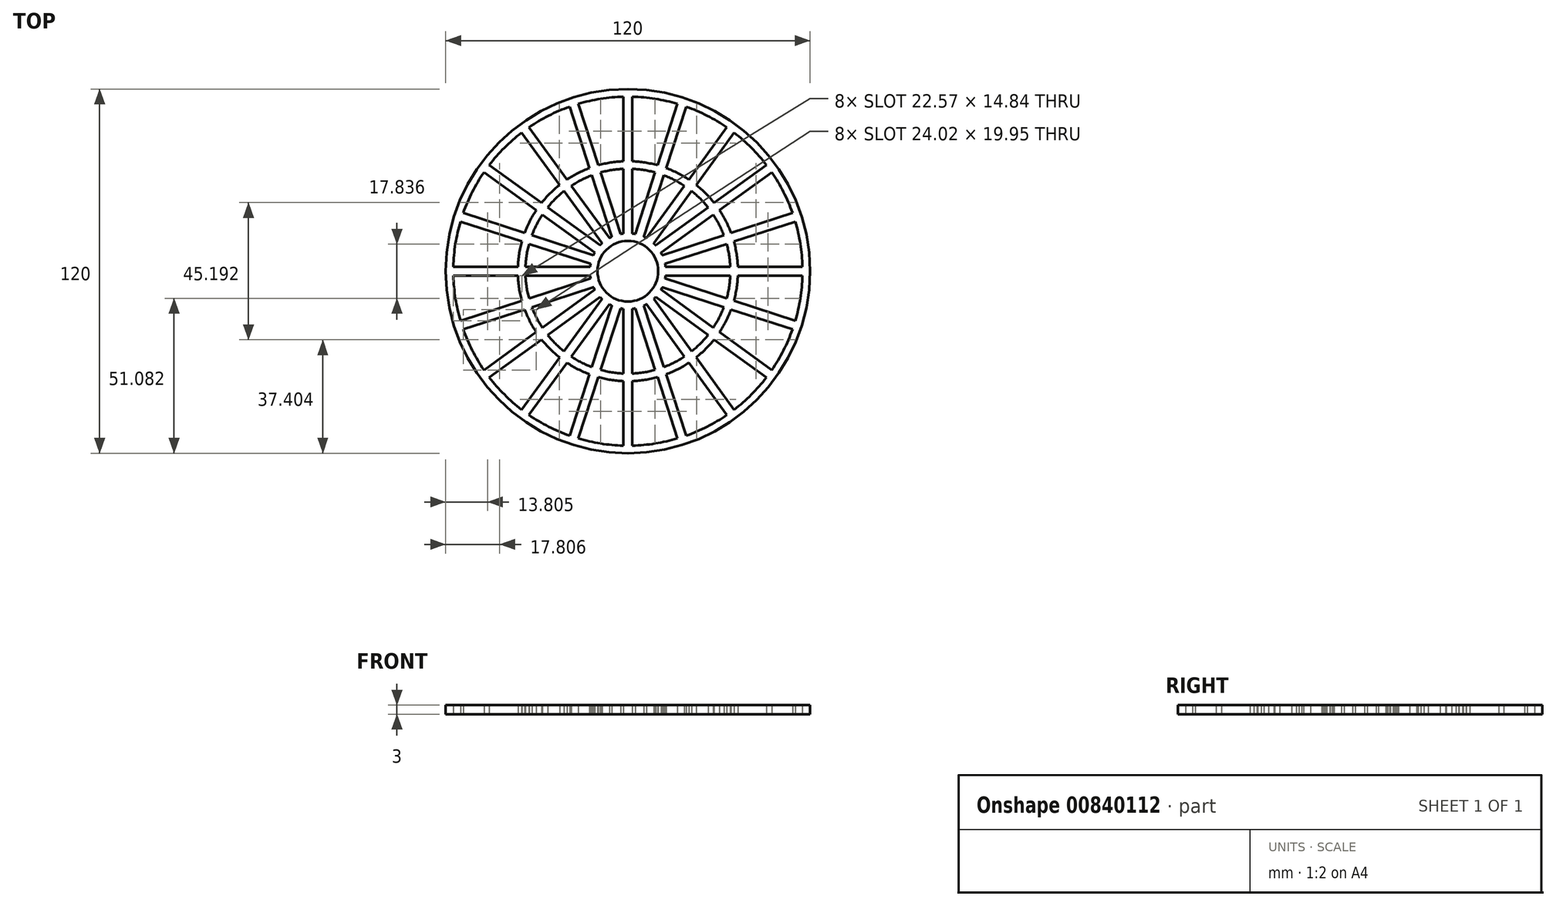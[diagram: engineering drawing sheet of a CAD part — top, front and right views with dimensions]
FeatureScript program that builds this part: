
annotation { "Feature Type Name" : "Feature", "Feature Type Description" : "" }
export const myFeature = defineFeature(function(context is Context, id is Id, definition is map)
    precondition{}
    {
        {
            var Q0;
            Q0=qCreatedBy(makeId("Top.planeOp"),FACE);
            var sketch = newSketch(context, id + "F0", { "sketchPlane" : qUnion([Q0])});
            skCircle(sketch, "E0", {"center": v(0, 0) * mm, "radius": 60 * mm});
            skCircle(sketch, "E1", {"center": v(0, 0) * mm, "radius": 10 * mm});
            skCircle(sketch, "E2", {"center": v(0, 0) * mm, "radius": 12.5 * mm});
            skCircle(sketch, "E3", {"center": v(0, 0) * mm, "radius": 57.5 * mm});
            skLineSegment(sketch, "E4.bottom", {"start": v(-57.5, 1.5) * mm, "end": v(0, 1.5) * mm});
            skLineSegment(sketch, "E4.top", {"start": v(-57.5, -1.5) * mm, "end": v(0, -1.5) * mm});
            skLineSegment(sketch, "E4.left", {"start": v(-57.5, 1.5) * mm, "end": v(-57.5, -1.5) * mm});
            skLineSegment(sketch, "E4.right", {"start": v(0, 1.5) * mm, "end": v(0, -1.5) * mm});
            skLineSegment(sketch, "E5.1.0", {"start": v(-55.15, -16.34) * mm, "end": v(-0.46, 1.43) * mm});
            skLineSegment(sketch, "E5.1.1", {"start": v(-54.22, -19.2) * mm, "end": v(0.46, -1.43) * mm});
            skLineSegment(sketch, "E5.2.0", {"start": v(-47.4, -32.58) * mm, "end": v(-0.88, 1.21) * mm});
            skLineSegment(sketch, "E5.2.1", {"start": v(-45.64, -35.01) * mm, "end": v(0.88, -1.21) * mm});
            skLineSegment(sketch, "E5.3.0", {"start": v(-35.01, -45.64) * mm, "end": v(-1.21, 0.88) * mm});
            skLineSegment(sketch, "E5.3.1", {"start": v(-32.58, -47.4) * mm, "end": v(1.21, -0.88) * mm});
            skLineSegment(sketch, "E5.4.0", {"start": v(-19.2, -54.22) * mm, "end": v(-1.43, 0.46) * mm});
            skLineSegment(sketch, "E5.4.1", {"start": v(-16.34, -55.15) * mm, "end": v(1.43, -0.46) * mm});
            skLineSegment(sketch, "E5.5.0", {"start": v(-1.5, -57.5) * mm, "end": v(-1.5, 0) * mm});
            skLineSegment(sketch, "E5.5.1", {"start": v(1.5, -57.5) * mm, "end": v(1.5, 0) * mm});
            skLineSegment(sketch, "E5.6.0", {"start": v(16.34, -55.15) * mm, "end": v(-1.43, -0.46) * mm});
            skLineSegment(sketch, "E5.6.1", {"start": v(19.2, -54.22) * mm, "end": v(1.43, 0.46) * mm});
            skLineSegment(sketch, "E5.7.0", {"start": v(32.58, -47.4) * mm, "end": v(-1.21, -0.88) * mm});
            skLineSegment(sketch, "E5.7.1", {"start": v(35.01, -45.64) * mm, "end": v(1.21, 0.88) * mm});
            skLineSegment(sketch, "E5.8.0", {"start": v(45.64, -35.01) * mm, "end": v(-0.88, -1.21) * mm});
            skLineSegment(sketch, "E5.8.1", {"start": v(47.4, -32.58) * mm, "end": v(0.88, 1.21) * mm});
            skLineSegment(sketch, "E5.9.0", {"start": v(54.22, -19.2) * mm, "end": v(-0.46, -1.43) * mm});
            skLineSegment(sketch, "E5.9.1", {"start": v(55.15, -16.34) * mm, "end": v(0.46, 1.43) * mm});
            skLineSegment(sketch, "E5.10.0", {"start": v(57.5, -1.5) * mm, "end": v(0, -1.5) * mm});
            skLineSegment(sketch, "E5.10.1", {"start": v(57.5, 1.5) * mm, "end": v(0, 1.5) * mm});
            skLineSegment(sketch, "E5.11.0", {"start": v(55.15, 16.34) * mm, "end": v(0.46, -1.43) * mm});
            skLineSegment(sketch, "E5.11.1", {"start": v(54.22, 19.2) * mm, "end": v(-0.46, 1.43) * mm});
            skLineSegment(sketch, "E5.12.0", {"start": v(47.4, 32.58) * mm, "end": v(0.88, -1.21) * mm});
            skLineSegment(sketch, "E5.12.1", {"start": v(45.64, 35.01) * mm, "end": v(-0.88, 1.21) * mm});
            skLineSegment(sketch, "E5.13.0", {"start": v(35.01, 45.64) * mm, "end": v(1.21, -0.88) * mm});
            skLineSegment(sketch, "E5.13.1", {"start": v(32.58, 47.4) * mm, "end": v(-1.21, 0.88) * mm});
            skLineSegment(sketch, "E5.14.0", {"start": v(19.2, 54.22) * mm, "end": v(1.43, -0.46) * mm});
            skLineSegment(sketch, "E5.14.1", {"start": v(16.34, 55.15) * mm, "end": v(-1.43, 0.46) * mm});
            skCircle(sketch, "E6", {"center": v(0, 0) * mm, "radius": 33.75 * mm});
            skCircle(sketch, "E7", {"center": v(0, 0) * mm, "radius": 36.25 * mm});
            skLineSegment(sketch, "E8.1.15.0", {"start": v(1.5, 57.5) * mm, "end": v(1.5, 0) * mm});
            skLineSegment(sketch, "E8.3.15.0", {"start": v(-1.5, 57.5) * mm, "end": v(-1.5, 0) * mm});
            skLineSegment(sketch, "E8.1.16.0", {"start": v(-16.34, 55.15) * mm, "end": v(1.43, 0.46) * mm});
            skLineSegment(sketch, "E8.3.16.0", {"start": v(-19.2, 54.22) * mm, "end": v(-1.43, -0.46) * mm});
            skLineSegment(sketch, "E8.1.17.0", {"start": v(-32.58, 47.4) * mm, "end": v(1.21, 0.88) * mm});
            skLineSegment(sketch, "E8.3.17.0", {"start": v(-35.01, 45.64) * mm, "end": v(-1.21, -0.88) * mm});
            skLineSegment(sketch, "E8.1.18.0", {"start": v(-45.64, 35.01) * mm, "end": v(0.88, 1.21) * mm});
            skLineSegment(sketch, "E8.3.18.0", {"start": v(-47.4, 32.58) * mm, "end": v(-0.88, -1.21) * mm});
            skLineSegment(sketch, "E8.1.19.0", {"start": v(-54.22, 19.2) * mm, "end": v(0.46, 1.43) * mm});
            skLineSegment(sketch, "E8.3.19.0", {"start": v(-55.15, 16.34) * mm, "end": v(-0.46, -1.43) * mm});
            skSolve(sketch);
        }
        {
            var Q0;
            Q0=qCreatedBy(makeId("Top.planeOp"),FACE);
            var sketch = newSketch(context, id + "F1", { "sketchPlane" : qUnion([Q0])});
            skCircle(sketch, "E9", {"center": v(0, 0) * mm, "radius": 60 * mm});
            skCircle(sketch, "E10", {"center": v(0, 0) * mm, "radius": 10 * mm});
            skSolve(sketch);
        }
        {
            var Q0;
            Q0=makeQuery(id+"F1.imprint","IMPRINT",FACE,{"disambiguationData":[TD([[makeQuery(id+"F1.imprint","IMPRINT",EDGE,{"derivedFrom":sQuery(id+"F1.wireOp",EDGE,"E9")}),1.0]])]});
            extrude(context, id + "F2", {"entities" : qUnion([Q0]), "depth" : 3 * mm, "offsetDistance" : 25 * mm});
        }
        {
            var Q0;
            {var subQ0=sQuery(id+"F0.wireOp",EDGE,"E5.11.1");var subQ1=sQuery(id+"F0.wireOp",EDGE,"E2");var subQ2=makeQuery(id+"F0.imprint","INTERSECT",VERTEX,{"derivedFrom":[subQ1,subQ0]});Q0=makeQuery(id+"F0.imprint","IMPRINT",FACE,{"disambiguationData":[TD([[makeQuery(id+"F0.imprint","IMPRINT",EDGE,{"disambiguationData":[TD([[subQ2,-1.0]])],"derivedFrom":subQ1}),-1.0]])]});}
            var Q1;
            {var subQ0=sQuery(id+"F0.wireOp",EDGE,"E5.12.1");var subQ1=sQuery(id+"F0.wireOp",EDGE,"E2");var subQ2=makeQuery(id+"F0.imprint","INTERSECT",VERTEX,{"derivedFrom":[subQ1,subQ0]});Q1=makeQuery(id+"F0.imprint","IMPRINT",FACE,{"disambiguationData":[TD([[makeQuery(id+"F0.imprint","IMPRINT",EDGE,{"disambiguationData":[TD([[subQ2,-1.0]])],"derivedFrom":subQ1}),-1.0]])]});}
            var Q2;
            {var subQ0=sQuery(id+"F0.wireOp",EDGE,"E5.13.1");var subQ1=sQuery(id+"F0.wireOp",EDGE,"E2");var subQ2=makeQuery(id+"F0.imprint","INTERSECT",VERTEX,{"derivedFrom":[subQ1,subQ0]});Q2=makeQuery(id+"F0.imprint","IMPRINT",FACE,{"disambiguationData":[TD([[makeQuery(id+"F0.imprint","IMPRINT",EDGE,{"disambiguationData":[TD([[subQ2,-1.0]])],"derivedFrom":subQ1}),-1.0]])]});}
            var Q3;
            {var subQ0=sQuery(id+"F0.wireOp",EDGE,"E5.14.1");var subQ1=sQuery(id+"F0.wireOp",EDGE,"E2");var subQ2=makeQuery(id+"F0.imprint","INTERSECT",VERTEX,{"derivedFrom":[subQ1,subQ0]});Q3=makeQuery(id+"F0.imprint","IMPRINT",FACE,{"disambiguationData":[TD([[makeQuery(id+"F0.imprint","IMPRINT",EDGE,{"disambiguationData":[TD([[subQ2,-1.0]])],"derivedFrom":subQ1}),-1.0]])]});}
            var Q4;
            {var subQ0=sQuery(id+"F0.wireOp",EDGE,"E4.top");var subQ1=sQuery(id+"F0.wireOp",EDGE,"E2");var subQ2=makeQuery(id+"F0.imprint","INTERSECT",VERTEX,{"derivedFrom":[subQ1,subQ0]});Q4=makeQuery(id+"F0.imprint","IMPRINT",FACE,{"disambiguationData":[TD([[makeQuery(id+"F0.imprint","IMPRINT",EDGE,{"disambiguationData":[TD([[subQ2,-1.0]])],"derivedFrom":subQ1}),-1.0]])]});}
            var Q5;
            {var subQ0=sQuery(id+"F0.wireOp",EDGE,"E5.1.1");var subQ1=sQuery(id+"F0.wireOp",EDGE,"E2");var subQ2=makeQuery(id+"F0.imprint","INTERSECT",VERTEX,{"derivedFrom":[subQ1,subQ0]});Q5=makeQuery(id+"F0.imprint","IMPRINT",FACE,{"disambiguationData":[TD([[makeQuery(id+"F0.imprint","IMPRINT",EDGE,{"disambiguationData":[TD([[subQ2,-1.0]])],"derivedFrom":subQ1}),-1.0]])]});}
            var Q6;
            {var subQ0=sQuery(id+"F0.wireOp",EDGE,"E5.2.1");var subQ1=sQuery(id+"F0.wireOp",EDGE,"E2");var subQ2=makeQuery(id+"F0.imprint","INTERSECT",VERTEX,{"derivedFrom":[subQ1,subQ0]});Q6=makeQuery(id+"F0.imprint","IMPRINT",FACE,{"disambiguationData":[TD([[makeQuery(id+"F0.imprint","IMPRINT",EDGE,{"disambiguationData":[TD([[subQ2,-1.0]])],"derivedFrom":subQ1}),-1.0]])]});}
            var Q7;
            {var subQ0=sQuery(id+"F0.wireOp",EDGE,"E5.3.1");var subQ1=sQuery(id+"F0.wireOp",EDGE,"E2");var subQ2=makeQuery(id+"F0.imprint","INTERSECT",VERTEX,{"derivedFrom":[subQ1,subQ0]});Q7=makeQuery(id+"F0.imprint","IMPRINT",FACE,{"disambiguationData":[TD([[makeQuery(id+"F0.imprint","IMPRINT",EDGE,{"disambiguationData":[TD([[subQ2,-1.0]])],"derivedFrom":subQ1}),-1.0]])]});}
            var Q8;
            {var subQ0=sQuery(id+"F0.wireOp",EDGE,"E5.4.1");var subQ1=sQuery(id+"F0.wireOp",EDGE,"E2");var subQ2=makeQuery(id+"F0.imprint","INTERSECT",VERTEX,{"derivedFrom":[subQ1,subQ0]});Q8=makeQuery(id+"F0.imprint","IMPRINT",FACE,{"disambiguationData":[TD([[makeQuery(id+"F0.imprint","IMPRINT",EDGE,{"disambiguationData":[TD([[subQ2,-1.0]])],"derivedFrom":subQ1}),-1.0]])]});}
            var Q9;
            {var subQ0=sQuery(id+"F0.wireOp",EDGE,"E5.5.1");var subQ1=sQuery(id+"F0.wireOp",EDGE,"E2");var subQ2=makeQuery(id+"F0.imprint","INTERSECT",VERTEX,{"derivedFrom":[subQ1,subQ0]});Q9=makeQuery(id+"F0.imprint","IMPRINT",FACE,{"disambiguationData":[TD([[makeQuery(id+"F0.imprint","IMPRINT",EDGE,{"disambiguationData":[TD([[subQ2,-1.0]])],"derivedFrom":subQ1}),-1.0]])]});}
            var Q10;
            {var subQ0=sQuery(id+"F0.wireOp",EDGE,"E5.6.1");var subQ1=sQuery(id+"F0.wireOp",EDGE,"E2");var subQ2=makeQuery(id+"F0.imprint","INTERSECT",VERTEX,{"derivedFrom":[subQ1,subQ0]});Q10=makeQuery(id+"F0.imprint","IMPRINT",FACE,{"disambiguationData":[TD([[makeQuery(id+"F0.imprint","IMPRINT",EDGE,{"disambiguationData":[TD([[subQ2,-1.0]])],"derivedFrom":subQ1}),-1.0]])]});}
            var Q11;
            {var subQ0=sQuery(id+"F0.wireOp",EDGE,"E5.8.0");var subQ1=sQuery(id+"F0.wireOp",EDGE,"E2");var subQ2=makeQuery(id+"F0.imprint","INTERSECT",VERTEX,{"derivedFrom":[subQ1,subQ0]});Q11=makeQuery(id+"F0.imprint","IMPRINT",FACE,{"disambiguationData":[TD([[makeQuery(id+"F0.imprint","IMPRINT",EDGE,{"disambiguationData":[TD([[subQ2,1.0]])],"derivedFrom":subQ1}),-1.0]])]});}
            var Q12;
            {var subQ0=sQuery(id+"F0.wireOp",EDGE,"E5.8.1");var subQ1=sQuery(id+"F0.wireOp",EDGE,"E2");var subQ2=makeQuery(id+"F0.imprint","INTERSECT",VERTEX,{"derivedFrom":[subQ1,subQ0]});Q12=makeQuery(id+"F0.imprint","IMPRINT",FACE,{"disambiguationData":[TD([[makeQuery(id+"F0.imprint","IMPRINT",EDGE,{"disambiguationData":[TD([[subQ2,-1.0]])],"derivedFrom":subQ1}),-1.0]])]});}
            var Q13;
            {var subQ0=sQuery(id+"F0.wireOp",EDGE,"E5.10.1");var subQ1=sQuery(id+"F0.wireOp",EDGE,"E2");var subQ2=makeQuery(id+"F0.imprint","INTERSECT",VERTEX,{"derivedFrom":[subQ1,subQ0]});Q13=makeQuery(id+"F0.imprint","IMPRINT",FACE,{"disambiguationData":[TD([[makeQuery(id+"F0.imprint","IMPRINT",EDGE,{"disambiguationData":[TD([[subQ2,-1.0]])],"derivedFrom":subQ1}),-1.0]])]});}
            var Q14;
            {var subQ0=sQuery(id+"F0.wireOp",EDGE,"E5.9.1");var subQ1=sQuery(id+"F0.wireOp",EDGE,"E2");var subQ2=makeQuery(id+"F0.imprint","INTERSECT",VERTEX,{"derivedFrom":[subQ1,subQ0]});Q14=makeQuery(id+"F0.imprint","IMPRINT",FACE,{"disambiguationData":[TD([[makeQuery(id+"F0.imprint","IMPRINT",EDGE,{"disambiguationData":[TD([[subQ2,-1.0]])],"derivedFrom":subQ1}),-1.0]])]});}
            var Q15;
            {var subQ0=sQuery(id+"F0.wireOp",EDGE,"E8.3.19.0");var subQ1=sQuery(id+"F0.wireOp",EDGE,"E2");var subQ2=makeQuery(id+"F0.imprint","INTERSECT",VERTEX,{"derivedFrom":[subQ1,subQ0]});Q15=makeQuery(id+"F0.imprint","IMPRINT",FACE,{"disambiguationData":[TD([[makeQuery(id+"F0.imprint","IMPRINT",EDGE,{"disambiguationData":[TD([[subQ2,-1.0]])],"derivedFrom":subQ1}),-1.0]])]});}
            var Q16;
            {var subQ0=sQuery(id+"F0.wireOp",EDGE,"E8.3.18.0");var subQ1=sQuery(id+"F0.wireOp",EDGE,"E2");var subQ2=makeQuery(id+"F0.imprint","INTERSECT",VERTEX,{"derivedFrom":[subQ1,subQ0]});Q16=makeQuery(id+"F0.imprint","IMPRINT",FACE,{"disambiguationData":[TD([[makeQuery(id+"F0.imprint","IMPRINT",EDGE,{"disambiguationData":[TD([[subQ2,-1.0]])],"derivedFrom":subQ1}),-1.0]])]});}
            var Q17;
            {var subQ0=sQuery(id+"F0.wireOp",EDGE,"E8.3.17.0");var subQ1=sQuery(id+"F0.wireOp",EDGE,"E2");var subQ2=makeQuery(id+"F0.imprint","INTERSECT",VERTEX,{"derivedFrom":[subQ1,subQ0]});Q17=makeQuery(id+"F0.imprint","IMPRINT",FACE,{"disambiguationData":[TD([[makeQuery(id+"F0.imprint","IMPRINT",EDGE,{"disambiguationData":[TD([[subQ2,-1.0]])],"derivedFrom":subQ1}),-1.0]])]});}
            var Q18;
            {var subQ0=sQuery(id+"F0.wireOp",EDGE,"E8.3.16.0");var subQ1=sQuery(id+"F0.wireOp",EDGE,"E2");var subQ2=makeQuery(id+"F0.imprint","INTERSECT",VERTEX,{"derivedFrom":[subQ1,subQ0]});Q18=makeQuery(id+"F0.imprint","IMPRINT",FACE,{"disambiguationData":[TD([[makeQuery(id+"F0.imprint","IMPRINT",EDGE,{"disambiguationData":[TD([[subQ2,-1.0]])],"derivedFrom":subQ1}),-1.0]])]});}
            var Q19;
            {var subQ0=sQuery(id+"F0.wireOp",EDGE,"E8.3.15.0");var subQ1=sQuery(id+"F0.wireOp",EDGE,"E2");var subQ2=makeQuery(id+"F0.imprint","INTERSECT",VERTEX,{"derivedFrom":[subQ1,subQ0]});Q19=makeQuery(id+"F0.imprint","IMPRINT",FACE,{"disambiguationData":[TD([[makeQuery(id+"F0.imprint","IMPRINT",EDGE,{"disambiguationData":[TD([[subQ2,-1.0]])],"derivedFrom":subQ1}),-1.0]])]});}
            var Q20;
            {var subQ0=sQuery(id+"F0.wireOp",EDGE,"E8.3.19.0");var subQ1=sQuery(id+"F0.wireOp",EDGE,"E3");var subQ2=makeQuery(id+"F0.imprint","INTERSECT",VERTEX,{"derivedFrom":[subQ1,subQ0]});Q20=makeQuery(id+"F0.imprint","IMPRINT",FACE,{"disambiguationData":[TD([[makeQuery(id+"F0.imprint","IMPRINT",EDGE,{"disambiguationData":[TD([[subQ2,-1.0]])],"derivedFrom":subQ1}),1.0]])]});}
            var Q21;
            {var subQ0=sQuery(id+"F0.wireOp",EDGE,"E5.1.0");var subQ1=sQuery(id+"F0.wireOp",EDGE,"E3");var subQ2=makeQuery(id+"F0.imprint","INTERSECT",VERTEX,{"derivedFrom":[subQ1,subQ0]});Q21=makeQuery(id+"F0.imprint","IMPRINT",FACE,{"disambiguationData":[TD([[makeQuery(id+"F0.imprint","IMPRINT",EDGE,{"disambiguationData":[TD([[subQ2,1.0]])],"derivedFrom":subQ1}),1.0]])]});}
            var Q22;
            {var subQ0=sQuery(id+"F0.wireOp",EDGE,"E5.1.1");var subQ1=sQuery(id+"F0.wireOp",EDGE,"E3");var subQ2=makeQuery(id+"F0.imprint","INTERSECT",VERTEX,{"derivedFrom":[subQ1,subQ0]});Q22=makeQuery(id+"F0.imprint","IMPRINT",FACE,{"disambiguationData":[TD([[makeQuery(id+"F0.imprint","IMPRINT",EDGE,{"disambiguationData":[TD([[subQ2,-1.0]])],"derivedFrom":subQ1}),1.0]])]});}
            var Q23;
            {var subQ0=sQuery(id+"F0.wireOp",EDGE,"E5.2.1");var subQ1=sQuery(id+"F0.wireOp",EDGE,"E3");var subQ2=makeQuery(id+"F0.imprint","INTERSECT",VERTEX,{"derivedFrom":[subQ1,subQ0]});Q23=makeQuery(id+"F0.imprint","IMPRINT",FACE,{"disambiguationData":[TD([[makeQuery(id+"F0.imprint","IMPRINT",EDGE,{"disambiguationData":[TD([[subQ2,-1.0]])],"derivedFrom":subQ1}),1.0]])]});}
            var Q24;
            {var subQ0=sQuery(id+"F0.wireOp",EDGE,"E5.3.1");var subQ1=sQuery(id+"F0.wireOp",EDGE,"E3");var subQ2=makeQuery(id+"F0.imprint","INTERSECT",VERTEX,{"derivedFrom":[subQ1,subQ0]});Q24=makeQuery(id+"F0.imprint","IMPRINT",FACE,{"disambiguationData":[TD([[makeQuery(id+"F0.imprint","IMPRINT",EDGE,{"disambiguationData":[TD([[subQ2,-1.0]])],"derivedFrom":subQ1}),1.0]])]});}
            var Q25;
            {var subQ0=sQuery(id+"F0.wireOp",EDGE,"E5.4.1");var subQ1=sQuery(id+"F0.wireOp",EDGE,"E3");var subQ2=makeQuery(id+"F0.imprint","INTERSECT",VERTEX,{"derivedFrom":[subQ1,subQ0]});Q25=makeQuery(id+"F0.imprint","IMPRINT",FACE,{"disambiguationData":[TD([[makeQuery(id+"F0.imprint","IMPRINT",EDGE,{"disambiguationData":[TD([[subQ2,-1.0]])],"derivedFrom":subQ1}),1.0]])]});}
            var Q26;
            {var subQ0=sQuery(id+"F0.wireOp",EDGE,"E5.5.1");var subQ1=sQuery(id+"F0.wireOp",EDGE,"E3");var subQ2=makeQuery(id+"F0.imprint","INTERSECT",VERTEX,{"derivedFrom":[subQ1,subQ0]});Q26=makeQuery(id+"F0.imprint","IMPRINT",FACE,{"disambiguationData":[TD([[makeQuery(id+"F0.imprint","IMPRINT",EDGE,{"disambiguationData":[TD([[subQ2,-1.0]])],"derivedFrom":subQ1}),1.0]])]});}
            var Q27;
            {var subQ0=sQuery(id+"F0.wireOp",EDGE,"E5.6.1");var subQ1=sQuery(id+"F0.wireOp",EDGE,"E3");var subQ2=makeQuery(id+"F0.imprint","INTERSECT",VERTEX,{"derivedFrom":[subQ1,subQ0]});Q27=makeQuery(id+"F0.imprint","IMPRINT",FACE,{"disambiguationData":[TD([[makeQuery(id+"F0.imprint","IMPRINT",EDGE,{"disambiguationData":[TD([[subQ2,-1.0]])],"derivedFrom":subQ1}),1.0]])]});}
            var Q28;
            {var subQ0=sQuery(id+"F0.wireOp",EDGE,"E5.7.1");var subQ1=sQuery(id+"F0.wireOp",EDGE,"E3");var subQ2=makeQuery(id+"F0.imprint","INTERSECT",VERTEX,{"derivedFrom":[subQ1,subQ0]});Q28=makeQuery(id+"F0.imprint","IMPRINT",FACE,{"disambiguationData":[TD([[makeQuery(id+"F0.imprint","IMPRINT",EDGE,{"disambiguationData":[TD([[subQ2,-1.0]])],"derivedFrom":subQ1}),1.0]])]});}
            var Q29;
            {var subQ0=sQuery(id+"F0.wireOp",EDGE,"E5.8.1");var subQ1=sQuery(id+"F0.wireOp",EDGE,"E3");var subQ2=makeQuery(id+"F0.imprint","INTERSECT",VERTEX,{"derivedFrom":[subQ1,subQ0]});Q29=makeQuery(id+"F0.imprint","IMPRINT",FACE,{"disambiguationData":[TD([[makeQuery(id+"F0.imprint","IMPRINT",EDGE,{"disambiguationData":[TD([[subQ2,-1.0]])],"derivedFrom":subQ1}),1.0]])]});}
            var Q30;
            {var subQ0=sQuery(id+"F0.wireOp",EDGE,"E5.9.1");var subQ1=sQuery(id+"F0.wireOp",EDGE,"E3");var subQ2=makeQuery(id+"F0.imprint","INTERSECT",VERTEX,{"derivedFrom":[subQ1,subQ0]});Q30=makeQuery(id+"F0.imprint","IMPRINT",FACE,{"disambiguationData":[TD([[makeQuery(id+"F0.imprint","IMPRINT",EDGE,{"disambiguationData":[TD([[subQ2,-1.0]])],"derivedFrom":subQ1}),1.0]])]});}
            var Q31;
            {var subQ0=sQuery(id+"F0.wireOp",EDGE,"E5.11.0");var subQ1=sQuery(id+"F0.wireOp",EDGE,"E3");var subQ2=makeQuery(id+"F0.imprint","INTERSECT",VERTEX,{"derivedFrom":[subQ1,subQ0]});Q31=makeQuery(id+"F0.imprint","IMPRINT",FACE,{"disambiguationData":[TD([[makeQuery(id+"F0.imprint","IMPRINT",EDGE,{"disambiguationData":[TD([[subQ2,1.0]])],"derivedFrom":subQ1}),1.0]])]});}
            var Q32;
            {var subQ0=sQuery(id+"F0.wireOp",EDGE,"E5.11.1");var subQ1=sQuery(id+"F0.wireOp",EDGE,"E3");var subQ2=makeQuery(id+"F0.imprint","INTERSECT",VERTEX,{"derivedFrom":[subQ1,subQ0]});Q32=makeQuery(id+"F0.imprint","IMPRINT",FACE,{"disambiguationData":[TD([[makeQuery(id+"F0.imprint","IMPRINT",EDGE,{"disambiguationData":[TD([[subQ2,-1.0]])],"derivedFrom":subQ1}),1.0]])]});}
            var Q33;
            {var subQ0=sQuery(id+"F0.wireOp",EDGE,"E5.12.1");var subQ1=sQuery(id+"F0.wireOp",EDGE,"E3");var subQ2=makeQuery(id+"F0.imprint","INTERSECT",VERTEX,{"derivedFrom":[subQ1,subQ0]});Q33=makeQuery(id+"F0.imprint","IMPRINT",FACE,{"disambiguationData":[TD([[makeQuery(id+"F0.imprint","IMPRINT",EDGE,{"disambiguationData":[TD([[subQ2,-1.0]])],"derivedFrom":subQ1}),1.0]])]});}
            var Q34;
            {var subQ0=sQuery(id+"F0.wireOp",EDGE,"E5.13.1");var subQ1=sQuery(id+"F0.wireOp",EDGE,"E3");var subQ2=makeQuery(id+"F0.imprint","INTERSECT",VERTEX,{"derivedFrom":[subQ1,subQ0]});Q34=makeQuery(id+"F0.imprint","IMPRINT",FACE,{"disambiguationData":[TD([[makeQuery(id+"F0.imprint","IMPRINT",EDGE,{"disambiguationData":[TD([[subQ2,-1.0]])],"derivedFrom":subQ1}),1.0]])]});}
            var Q35;
            {var subQ0=sQuery(id+"F0.wireOp",EDGE,"E5.14.1");var subQ1=sQuery(id+"F0.wireOp",EDGE,"E3");var subQ2=makeQuery(id+"F0.imprint","INTERSECT",VERTEX,{"derivedFrom":[subQ1,subQ0]});Q35=makeQuery(id+"F0.imprint","IMPRINT",FACE,{"disambiguationData":[TD([[makeQuery(id+"F0.imprint","IMPRINT",EDGE,{"disambiguationData":[TD([[subQ2,-1.0]])],"derivedFrom":subQ1}),1.0]])]});}
            var Q36;
            {var subQ0=sQuery(id+"F0.wireOp",EDGE,"E8.3.15.0");var subQ1=sQuery(id+"F0.wireOp",EDGE,"E3");var subQ2=makeQuery(id+"F0.imprint","INTERSECT",VERTEX,{"derivedFrom":[subQ1,subQ0]});Q36=makeQuery(id+"F0.imprint","IMPRINT",FACE,{"disambiguationData":[TD([[makeQuery(id+"F0.imprint","IMPRINT",EDGE,{"disambiguationData":[TD([[subQ2,-1.0]])],"derivedFrom":subQ1}),1.0]])]});}
            var Q37;
            {var subQ0=sQuery(id+"F0.wireOp",EDGE,"E8.3.16.0");var subQ1=sQuery(id+"F0.wireOp",EDGE,"E3");var subQ2=makeQuery(id+"F0.imprint","INTERSECT",VERTEX,{"derivedFrom":[subQ1,subQ0]});Q37=makeQuery(id+"F0.imprint","IMPRINT",FACE,{"disambiguationData":[TD([[makeQuery(id+"F0.imprint","IMPRINT",EDGE,{"disambiguationData":[TD([[subQ2,-1.0]])],"derivedFrom":subQ1}),1.0]])]});}
            var Q38;
            {var subQ0=sQuery(id+"F0.wireOp",EDGE,"E8.3.17.0");var subQ1=sQuery(id+"F0.wireOp",EDGE,"E3");var subQ2=makeQuery(id+"F0.imprint","INTERSECT",VERTEX,{"derivedFrom":[subQ1,subQ0]});Q38=makeQuery(id+"F0.imprint","IMPRINT",FACE,{"disambiguationData":[TD([[makeQuery(id+"F0.imprint","IMPRINT",EDGE,{"disambiguationData":[TD([[subQ2,-1.0]])],"derivedFrom":subQ1}),1.0]])]});}
            var Q39;
            {var subQ0=sQuery(id+"F0.wireOp",EDGE,"E8.3.18.0");var subQ1=sQuery(id+"F0.wireOp",EDGE,"E3");var subQ2=makeQuery(id+"F0.imprint","INTERSECT",VERTEX,{"derivedFrom":[subQ1,subQ0]});Q39=makeQuery(id+"F0.imprint","IMPRINT",FACE,{"disambiguationData":[TD([[makeQuery(id+"F0.imprint","IMPRINT",EDGE,{"disambiguationData":[TD([[subQ2,-1.0]])],"derivedFrom":subQ1}),1.0]])]});}
            extrude(context, id + "F3", {"entities" : qUnion([Q0, Q1, Q2, Q3, Q4, Q5, Q6, Q7, Q8, Q9, Q10, Q11, Q12, Q13, Q14, Q15, Q16, Q17, Q18, Q19, Q20, Q21, Q22, Q23, Q24, Q25, Q26, Q27, Q28, Q29, Q30, Q31, Q32, Q33, Q34, Q35, Q36, Q37, Q38, Q39]), "operationType" : NewBodyOperationType.REMOVE, "depth" : 25 * mm, "offsetDistance" : 25 * mm});
        }
    });
